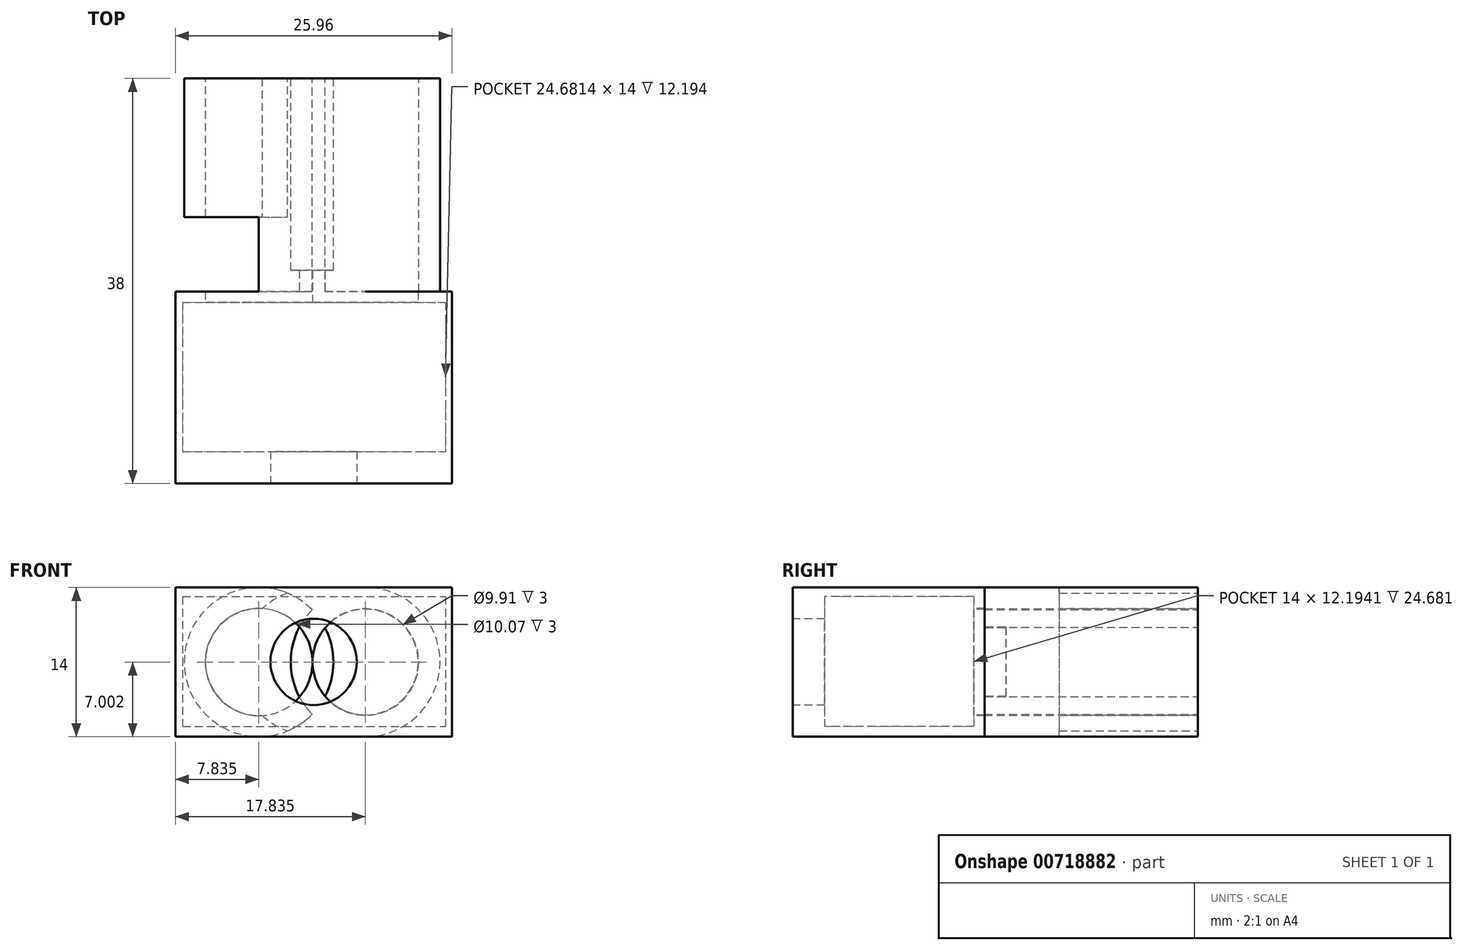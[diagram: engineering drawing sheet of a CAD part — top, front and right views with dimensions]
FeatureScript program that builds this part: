
annotation { "Feature Type Name" : "Feature", "Feature Type Description" : "" }
export const myFeature = defineFeature(function(context is Context, id is Id, definition is map)
    precondition{}
    {
        {
            var Q0;
            Q0=qCreatedBy(makeId("Front.planeOp"),FACE);
            var sketch = newSketch(context, id + "F0", { "sketchPlane" : qUnion([Q0])});
            skCircle(sketch, "E0", {"center": v(-25.75, 9.56) * mm, "radius": 5 * mm});
            skCircle(sketch, "E1", {"center": v(-15.75, 9.56) * mm, "radius": 5 * mm});
            skCircle(sketch, "E2.0", {"center": v(-25.75, 9.56) * mm, "radius": 7 * mm});
            skCircle(sketch, "E3.0", {"center": v(-15.75, 9.56) * mm, "radius": 7 * mm});
            skLineSegment(sketch, "E4", {"start": v(-25.75, 16.56) * mm, "end": v(-15.75, 16.56) * mm});
            skLineSegment(sketch, "E5", {"start": v(-25.75, 2.56) * mm, "end": v(-15.75, 2.56) * mm});
            skSolve(sketch);
        }
        {
            var Q0;
            Q0=qSketchRegion(id+"F0",true);
            extrude(context, id + "F1", {"entities" : qUnion([Q0]), "depth" : 13 * mm, "offsetDistance" : 25 * mm});
        }
        {
            var Q0;
            Q0=makeQuery(id+"F1.opExtrude","CAP_FACE",FACE,{"disambiguationData":[OSD([sQuery(id+"F0.wireOp",EDGE,"E0"),sQuery(id+"F0.wireOp",EDGE,"E1"),sQuery(id+"F0.wireOp",EDGE,"E2.0"),sQuery(id+"F0.wireOp",EDGE,"E3.0"),sQuery(id+"F0.wireOp",EDGE,"E4"),sQuery(id+"F0.wireOp",EDGE,"E5")])],"isStart":false});
            var sketch = newSketch(context, id + "F2", { "sketchPlane" : qUnion([Q0])});
            skCircle(sketch, "E6", {"center": v(-20.75, 9.56) * mm, "radius": 6.85 * mm});
            skPoint(sketch, "E6.centerSnap0", {"position": v(-10.75, 9.56) * mm});
            skSolve(sketch);
        }
        {
            var Q0;
            Q0=qSketchRegion(id+"F2",true);
            extrude(context, id + "F3", {"entities" : qUnion([Q0]), "operationType" : NewBodyOperationType.REMOVE, "oppositeDirection" : true, "depth" : 30 * mm, "offsetDistance" : 25 * mm});
        }
        {
            var Q0;
            {var subQ2=sQuery(id+"F0.wireOp",EDGE,"E2.0");var subQ4=sQuery(id+"F0.wireOp",EDGE,"E1");var subQ5=makeQuery(id+"F0.imprint","INTERSECT",VERTEX,{"disambiguationData":[OD(0.0)],"derivedFrom":[subQ4,subQ2]});Q0=makeQuery(id+"F0.imprint","IMPRINT",FACE,{"disambiguationData":[TD([[makeQuery(id+"F0.imprint","IMPRINT",EDGE,{"disambiguationData":[TD([[subQ5,1.0]])],"derivedFrom":subQ4}),-1.0]])]});}
            var Q1;
            {var subQ0=sQuery(id+"F0.wireOp",EDGE,"E1");var subQ1=sQuery(id+"F0.wireOp",EDGE,"E0");var subQ2=makeQuery(id+"F0.imprint","INTERSECT",VERTEX,{"disambiguationData":[OD(1.0)],"derivedFrom":[subQ1,subQ0]});Q1=makeQuery(id+"F0.imprint","IMPRINT",FACE,{"disambiguationData":[TD([[makeQuery(id+"F0.imprint","IMPRINT",EDGE,{"disambiguationData":[TD([[subQ2,1.0]])],"derivedFrom":subQ1}),-1.0]])]});}
            var Q2;
            {var subQ0=sQuery(id+"F0.wireOp",EDGE,"E1");var subQ1=sQuery(id+"F0.wireOp",EDGE,"E0");var subQ2=makeQuery(id+"F0.imprint","INTERSECT",VERTEX,{"disambiguationData":[OD(0.0)],"derivedFrom":[subQ1,subQ0]});Q2=makeQuery(id+"F0.imprint","IMPRINT",FACE,{"disambiguationData":[TD([[makeQuery(id+"F0.imprint","IMPRINT",EDGE,{"disambiguationData":[TD([[subQ2,-1.0]])],"derivedFrom":subQ1}),-1.0]])]});}
            var Q3;
            {var subQ0=sQuery(id+"F0.wireOp",EDGE,"E5");Q3=makeQuery(id+"F0.imprint","IMPRINT",FACE,{"disambiguationData":[TD([[makeQuery(id+"F0.imprint","IMPRINT",EDGE,{"derivedFrom":subQ0}),1.0]])]});}
            var Q4;
            {var subQ2=sQuery(id+"F0.wireOp",EDGE,"E3.0");var subQ6=sQuery(id+"F0.wireOp",EDGE,"E0");var subQ7=makeQuery(id+"F0.imprint","INTERSECT",VERTEX,{"disambiguationData":[OD(0.0)],"derivedFrom":[subQ6,subQ2]});Q4=makeQuery(id+"F0.imprint","IMPRINT",FACE,{"disambiguationData":[TD([[makeQuery(id+"F0.imprint","IMPRINT",EDGE,{"disambiguationData":[TD([[subQ7,-1.0]])],"derivedFrom":subQ6}),-1.0]])]});}
            var Q5;
            {var subQ0=sQuery(id+"F0.wireOp",EDGE,"E4");Q5=makeQuery(id+"F0.imprint","IMPRINT",FACE,{"disambiguationData":[TD([[makeQuery(id+"F0.imprint","IMPRINT",EDGE,{"derivedFrom":subQ0}),-1.0]])]});}
            var Q6;
            {var subQ0=sQuery(id+"F0.wireOp",EDGE,"E1");var subQ1=sQuery(id+"F0.wireOp",EDGE,"E0");var subQ2=makeQuery(id+"F0.imprint","INTERSECT",VERTEX,{"disambiguationData":[OD(0.0)],"derivedFrom":[subQ1,subQ0]});Q6=makeQuery(id+"F0.imprint","IMPRINT",FACE,{"disambiguationData":[TD([[makeQuery(id+"F0.imprint","IMPRINT",EDGE,{"disambiguationData":[TD([[subQ2,-1.0]])],"derivedFrom":subQ1}),1.0]])]});}
            var Q7;
            {var subQ0=sQuery(id+"F0.wireOp",EDGE,"E1");var subQ1=sQuery(id+"F0.wireOp",EDGE,"E0");var subQ2=makeQuery(id+"F0.imprint","INTERSECT",VERTEX,{"disambiguationData":[OD(0.0)],"derivedFrom":[subQ1,subQ0]});Q7=makeQuery(id+"F0.imprint","IMPRINT",FACE,{"disambiguationData":[TD([[makeQuery(id+"F0.imprint","IMPRINT",EDGE,{"disambiguationData":[TD([[subQ2,1.0]])],"derivedFrom":subQ0}),1.0]])]});}
            extrude(context, id + "F4", {"entities" : qUnion([Q0, Q1, Q2, Q3, Q4, Q5, Q6, Q7]), "operationType" : NewBodyOperationType.ADD, "depth" : 20 * mm, "offsetDistance" : 25 * mm});
        }
        {
            var Q0;
            Q0=makeQuery(id+"F4.opExtrude","CAP_FACE",FACE,{"disambiguationData":[OSD([sQuery(id+"F0.wireOp",EDGE,"E0"),sQuery(id+"F0.wireOp",EDGE,"E1"),sQuery(id+"F0.wireOp",EDGE,"E2.0"),sQuery(id+"F0.wireOp",EDGE,"E3.0"),sQuery(id+"F0.wireOp",EDGE,"E4"),sQuery(id+"F0.wireOp",EDGE,"E5")])],"isStart":false});
            var sketch = newSketch(context, id + "F5", { "sketchPlane" : qUnion([Q0])});
            skPoint(sketch, "E7.firstSnap0", {"position": v(-32.75, 9.56) * mm});
            skPoint(sketch, "E8.oppositeSnap0", {"position": v(-20.75, 16.56) * mm});
            skLineSegment(sketch, "E8.bottom", {"start": v(-33.58, 2.56) * mm, "end": v(-7.62, 2.56) * mm});
            skLineSegment(sketch, "E8.top", {"start": v(-33.58, 16.56) * mm, "end": v(-7.62, 16.56) * mm});
            skLineSegment(sketch, "E8.left", {"start": v(-33.58, 2.56) * mm, "end": v(-33.58, 16.56) * mm});
            skLineSegment(sketch, "E8.right", {"start": v(-7.62, 2.56) * mm, "end": v(-7.62, 16.56) * mm});
            skSolve(sketch);
        }
        {
            var Q0;
            Q0 = qSketchRegion(id + "F5", true);
            extrude(context, id + "F6", {"entities" : qUnion([Q0]), "operationType" : NewBodyOperationType.ADD, "depth" : 15 * mm, "offsetDistance" : 25 * mm});
        }
        {
            var Q0;
            Q0=makeQuery(id+"F6.opExtrude","CAP_FACE",FACE,{"disambiguationData":[OSD([sQuery(id+"F5.wireOp",EDGE,"E8.bottom"),sQuery(id+"F5.wireOp",EDGE,"E8.top"),sQuery(id+"F5.wireOp",EDGE,"E8.left"),sQuery(id+"F5.wireOp",EDGE,"E8.right")])],"isStart":false});
            var sketch = newSketch(context, id + "F7", { "sketchPlane" : qUnion([Q0])});
            skLineSegment(sketch, "E9.bottom", {"start": v(-32.9, 15.7) * mm, "end": v(-8.22, 15.7) * mm});
            skLineSegment(sketch, "E9.top", {"start": v(-32.9, 3.52) * mm, "end": v(-8.22, 3.52) * mm});
            skLineSegment(sketch, "E9.left", {"start": v(-32.9, 15.7) * mm, "end": v(-32.9, 3.52) * mm});
            skLineSegment(sketch, "E9.right", {"start": v(-8.22, 15.7) * mm, "end": v(-8.22, 3.52) * mm});
            skSolve(sketch);
        }
        {
            var Q0;
            Q0 = qSketchRegion(id + "F7", true);
            extrude(context, id + "F8", {"entities" : qUnion([Q0]), "operationType" : NewBodyOperationType.REMOVE, "oppositeDirection" : true, "depth" : 14 * mm, "offsetDistance" : 25 * mm});
        }
        {
            var Q0;
            Q0=makeQuery(id+"F8.boolean.opBoolean","COPY",FACE,{"derivedFrom":makeQuery(id+"F8.opExtrude","CAP_FACE",FACE,{"disambiguationData":[OSD([sQuery(id+"F7.wireOp",EDGE,"E9.bottom"),sQuery(id+"F7.wireOp",EDGE,"E9.top"),sQuery(id+"F7.wireOp",EDGE,"E9.left"),sQuery(id+"F7.wireOp",EDGE,"E9.right")])],"isStart":false})});
            var sketch = newSketch(context, id + "F9", { "sketchPlane" : qUnion([Q0])});
            skCircle(sketch, "E10", {"center": v(-25.75, 9.56) * mm, "radius": 5.03 * mm});
            skCircle(sketch, "E11", {"center": v(-15.75, 9.56) * mm, "radius": 4.96 * mm});
            skSolve(sketch);
        }
        {
            var Q0;
            Q0 = qSketchRegion(id + "F9", true);
            extrude(context, id + "F10", {"entities" : qUnion([Q0]), "operationType" : NewBodyOperationType.REMOVE, "oppositeDirection" : true, "depth" : 3 * mm, "offsetDistance" : 25 * mm});
        }
        {
            var Q0;
            Q0=makeQuery(id+"F6.opExtrude","CAP_FACE",FACE,{"disambiguationData":[OSD([sQuery(id+"F5.wireOp",EDGE,"E8.bottom"),sQuery(id+"F5.wireOp",EDGE,"E8.top"),sQuery(id+"F5.wireOp",EDGE,"E8.left"),sQuery(id+"F5.wireOp",EDGE,"E8.right")])],"isStart":false});
            var sketch = newSketch(context, id + "F11", { "sketchPlane" : qUnion([Q0])});
            skLineSegment(sketch, "E12.bottom", {"start": v(-33.58, 16.56) * mm, "end": v(-7.62, 16.56) * mm});
            skLineSegment(sketch, "E12.top", {"start": v(-33.58, 2.56) * mm, "end": v(-7.62, 2.56) * mm});
            skLineSegment(sketch, "E12.left", {"start": v(-33.58, 16.56) * mm, "end": v(-33.58, 2.56) * mm});
            skLineSegment(sketch, "E12.right", {"start": v(-7.62, 16.56) * mm, "end": v(-7.62, 2.56) * mm});
            skSolve(sketch);
        }
        {
            var Q0;
            Q0 = qSketchRegion(id + "F11", true);
            extrude(context, id + "F12", {"entities" : qUnion([Q0]), "operationType" : NewBodyOperationType.ADD, "depth" : 3 * mm, "offsetDistance" : 25 * mm});
        }
        {
            var Q0;
            Q0=makeQuery(id+"F12.opExtrude","CAP_FACE",FACE,{"disambiguationData":[OSD([sQuery(id+"F11.wireOp",EDGE,"E12.bottom"),sQuery(id+"F11.wireOp",EDGE,"E12.top"),sQuery(id+"F11.wireOp",EDGE,"E12.left"),sQuery(id+"F11.wireOp",EDGE,"E12.right")])],"isStart":false});
            var sketch = newSketch(context, id + "F13", { "sketchPlane" : qUnion([Q0])});
            skCircle(sketch, "E13", {"center": v(-20.6, 9.58) * mm, "radius": 4.05 * mm});
            skPoint(sketch, "E13.centerSnap0", {"position": v(-20.6, 16.56) * mm});
            skSolve(sketch);
        }
        {
            var Q0;
            Q0 = qSketchRegion(id + "F13", true);
            extrude(context, id + "F14", {"entities" : qUnion([Q0]), "operationType" : NewBodyOperationType.REMOVE, "oppositeDirection" : true, "depth" : 5 * mm, "offsetDistance" : 25 * mm});
        }
    });
